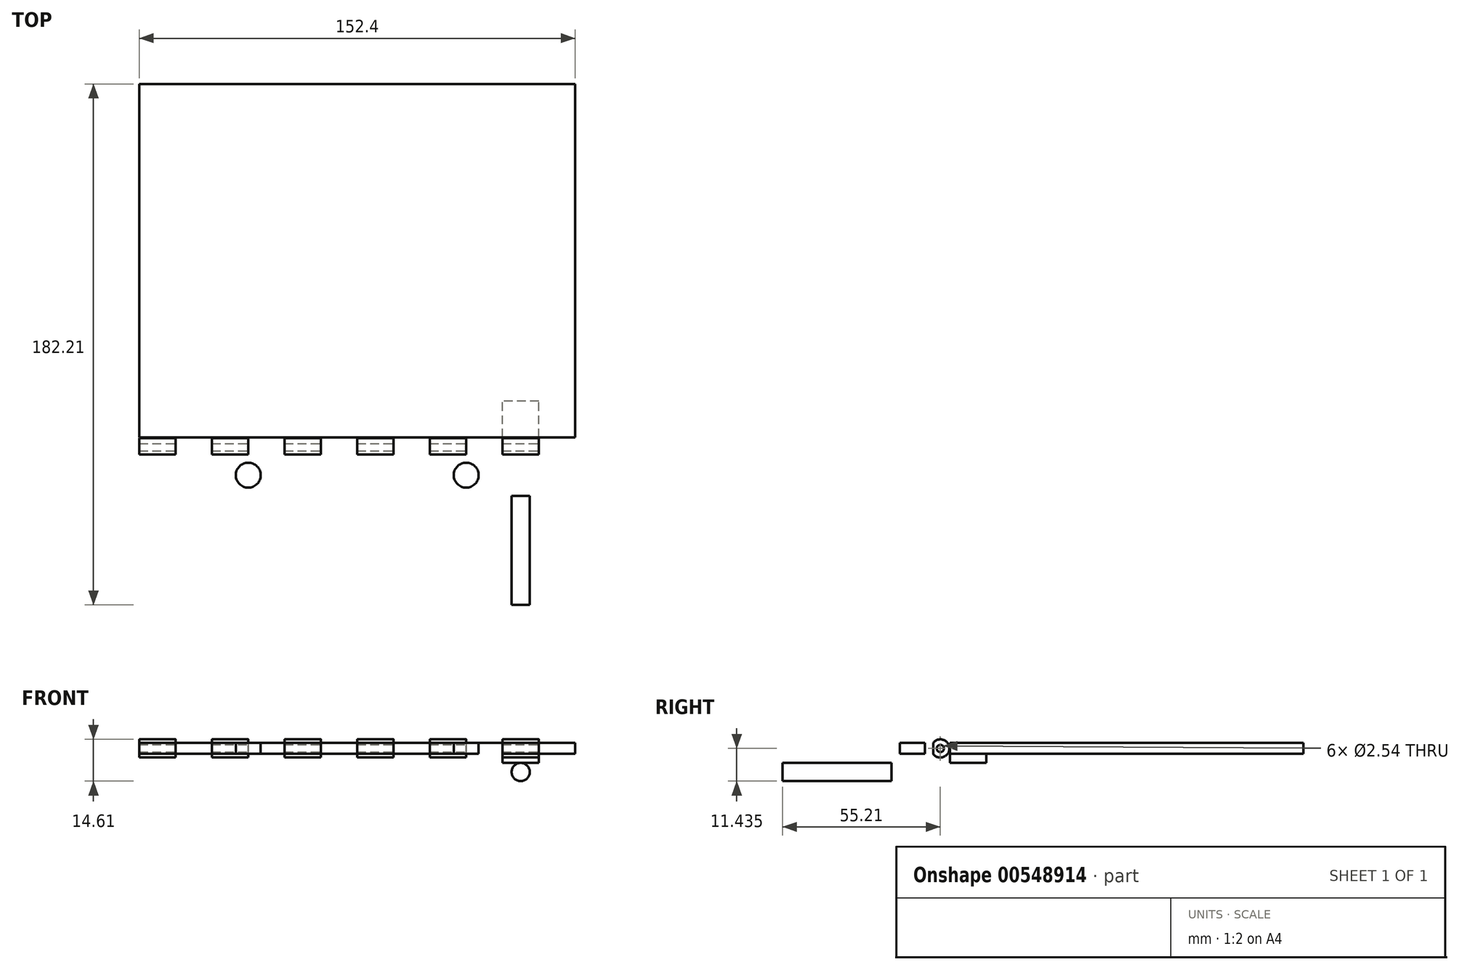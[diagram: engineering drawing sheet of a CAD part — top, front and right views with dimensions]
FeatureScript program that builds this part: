
annotation { "Feature Type Name" : "Feature", "Feature Type Description" : "" }
export const myFeature = defineFeature(function(context is Context, id is Id, definition is map)
    precondition{}
    {
        {
            var Q0;
            Q0=qCreatedBy(makeId("Top.planeOp"),FACE);
            var sketch = newSketch(context, id + "F0", { "sketchPlane" : qUnion([Q0])});
            skLineSegment(sketch, "E0.bottom", {"start": v(76.2, 63.5) * mm, "end": v(-76.2, 63.5) * mm});
            skLineSegment(sketch, "E0.top", {"start": v(76.2, -63.5) * mm, "end": v(-76.2, -63.5) * mm});
            skLineSegment(sketch, "E0.left", {"start": v(76.2, 63.5) * mm, "end": v(76.2, -63.5) * mm});
            skLineSegment(sketch, "E0.right", {"start": v(-76.2, 63.5) * mm, "end": v(-76.2, -63.5) * mm});
            skPoint(sketch, "E0.middle", {"position": v(0, 0) * mm});
            skSolve(sketch);
        }
        {
            var Q0;
            Q0=makeQuery(id+"F0.imprint","IMPRINT",FACE,{"disambiguationData":[TD([[makeQuery(id+"F0.imprint","IMPRINT",EDGE,{"derivedFrom":sQuery(id+"F0.wireOp",EDGE,"E0.bottom")}),1.0]])]});
            extrude(context, id + "F1", {"entities" : qUnion([Q0]), "depth" : 3.8 * mm, "offsetDistance" : 25.4 * mm});
        }
        {
            var Q0;
            Q0=makeQuery(id+"F1.opExtrude","SWEPT_FACE",FACE,{"disambiguationData":[OSD([sQuery(id+"F0.wireOp",EDGE,"E0.left")])]});
            var sketch = newSketch(context, id + "F2", { "sketchPlane" : qUnion([Q0])});
            skCircle(sketch, "E1", {"center": v(-63.5, 1.9) * mm, "radius": 3.18 * mm});
            skCircle(sketch, "E2", {"center": v(-63.5, 1.9) * mm, "radius": 1.27 * mm});
            skSolve(sketch);
        }
        {
            var Q0;
            {var subQ0=sQuery(id+"F2.wireOp",EDGE,"E2");var subQ1=makeQuery(id+"F1.opExtrude","SWEPT_EDGE",EDGE,{"disambiguationData":[OSD([sQuery(id+"F0.wireOp",EDGE,"E0.top"),sQuery(id+"F0.wireOp",EDGE,"E0.left")])]});var subQ2=makeQuery(id+"F2.imprint","INTERSECT",VERTEX,{"disambiguationData":[OD(0.0)],"derivedFrom":[subQ1,subQ0]});Q0=makeQuery(id+"F2.imprint","IMPRINT",FACE,{"disambiguationData":[TD([[makeQuery(id+"F2.imprint","IMPRINT",EDGE,{"disambiguationData":[TD([[subQ2,-1.0]])],"derivedFrom":subQ0}),1.0]])]});}
            extrude(context, id + "F3", {"entities" : qUnion([Q0]), "operationType" : NewBodyOperationType.REMOVE, "endBound" : BoundingType.THROUGH_ALL, "oppositeDirection" : true, "depth" : 25.4 * mm, "offsetDistance" : 25.4 * mm});
        }
        {
            var Q0;
            Q0 = qSketchRegion(id + "F2", true);
            var Q1;
            Q1=makeQuery(id+"F1.opExtrude","SWEPT_FACE",FACE,{"disambiguationData":[OSD([sQuery(id+"F0.wireOp",EDGE,"E0.right")])]});
            extrude(context, id + "F4", {"entities" : qUnion([Q0]), "operationType" : NewBodyOperationType.ADD, "endBound" : BoundingType.UP_TO_SURFACE, "oppositeDirection" : true, "depth" : 25.4 * mm, "endBoundEntityFace" : qUnion([Q1]), "offsetDistance" : 25.4 * mm});
        }
        {
            var Q0;
            Q0=qCreatedBy(makeId("Top.planeOp"),FACE);
            cPlane(context, id + "F5", {"entities" : qUnion([Q0]), "cplaneType" : CPlaneType.OFFSET, "offset" : 25.4 * mm, "width" : 152.4 * mm, "height" : 152.4 * mm});
        }
        {
            var Q0;
            Q0=qCreatedBy(id+"F5.planeOp",FACE);
            var sketch = newSketch(context, id + "F6", { "sketchPlane" : qUnion([Q0])});
            skLineSegment(sketch, "E3", {"start": v(63.5, -66.67) * mm, "end": v(50.8, -66.67) * mm});
            skLineSegment(sketch, "E4.0", {"start": v(-76.2, -60.96) * mm, "end": v(-76.2, -66.67) * mm});
            skLineSegment(sketch, "E5.bottom", {"start": v(-76.2, -66.67) * mm, "end": v(-63.5, -66.67) * mm});
            skLineSegment(sketch, "E5.top", {"start": v(-76.2, -60.07) * mm, "end": v(-63.5, -60.07) * mm});
            skLineSegment(sketch, "E5.left", {"start": v(-76.2, -66.67) * mm, "end": v(-76.2, -60.07) * mm});
            skLineSegment(sketch, "E5.right", {"start": v(-63.5, -66.67) * mm, "end": v(-63.5, -60.07) * mm});
            skLineSegment(sketch, "E6.1.0.0", {"start": v(-50.8, -60.07) * mm, "end": v(-38.1, -60.07) * mm});
            skLineSegment(sketch, "E6.1.0.1", {"start": v(-38.1, -66.67) * mm, "end": v(-38.1, -60.07) * mm});
            skLineSegment(sketch, "E6.1.0.2", {"start": v(-50.8, -66.67) * mm, "end": v(-38.1, -66.67) * mm});
            skLineSegment(sketch, "E6.1.0.3", {"start": v(-50.8, -66.67) * mm, "end": v(-50.8, -60.07) * mm});
            skLineSegment(sketch, "E6.2.0.0", {"start": v(-25.4, -60.07) * mm, "end": v(-12.7, -60.07) * mm});
            skLineSegment(sketch, "E6.2.0.1", {"start": v(-12.7, -66.67) * mm, "end": v(-12.7, -60.07) * mm});
            skLineSegment(sketch, "E6.2.0.2", {"start": v(-25.4, -66.67) * mm, "end": v(-12.7, -66.67) * mm});
            skLineSegment(sketch, "E6.2.0.3", {"start": v(-25.4, -66.67) * mm, "end": v(-25.4, -60.07) * mm});
            skLineSegment(sketch, "E6.3.0.0", {"start": v(0, -60.07) * mm, "end": v(12.7, -60.07) * mm});
            skLineSegment(sketch, "E6.3.0.1", {"start": v(12.7, -66.67) * mm, "end": v(12.7, -60.07) * mm});
            skLineSegment(sketch, "E6.3.0.2", {"start": v(0, -66.67) * mm, "end": v(12.7, -66.67) * mm});
            skLineSegment(sketch, "E6.3.0.3", {"start": v(0, -66.67) * mm, "end": v(0, -60.07) * mm});
            skLineSegment(sketch, "E6.4.0.0", {"start": v(25.4, -60.07) * mm, "end": v(38.1, -60.07) * mm});
            skLineSegment(sketch, "E6.4.0.1", {"start": v(38.1, -66.67) * mm, "end": v(38.1, -60.07) * mm});
            skLineSegment(sketch, "E6.4.0.2", {"start": v(25.4, -66.67) * mm, "end": v(38.1, -66.67) * mm});
            skLineSegment(sketch, "E6.4.0.3", {"start": v(25.4, -66.67) * mm, "end": v(25.4, -60.07) * mm});
            skLineSegment(sketch, "E6.5.0.0", {"start": v(50.8, -60.07) * mm, "end": v(63.5, -60.07) * mm});
            skLineSegment(sketch, "E6.5.0.1", {"start": v(63.5, -66.67) * mm, "end": v(63.5, -60.07) * mm});
            skLineSegment(sketch, "E6.5.0.2", {"start": v(50.8, -66.67) * mm, "end": v(63.5, -66.67) * mm});
            skLineSegment(sketch, "E6.5.0.3", {"start": v(50.8, -66.67) * mm, "end": v(50.8, -60.07) * mm});
            skLineSegment(sketch, "E6.direction1", {"start": v(-76.2, -60.07) * mm, "end": v(-63.5, -60.07) * mm, "construction": true});
            skPoint(sketch, "E7.0.start.orphan", {"position": v(76.2, -60.96) * mm});
            skPoint(sketch, "E8.0.end.orphan", {"position": v(76.2, -66.67) * mm});
            skLineSegment(sketch, "E9.trimOffspring", {"start": v(38.1, -66.67) * mm, "end": v(25.4, -66.67) * mm});
            skLineSegment(sketch, "E10.trimOffspring", {"start": v(12.7, -66.67) * mm, "end": v(0, -66.67) * mm});
            skLineSegment(sketch, "E11.trimOffspring", {"start": v(-12.7, -66.67) * mm, "end": v(-25.4, -66.67) * mm});
            skLineSegment(sketch, "E12.trimOffspring", {"start": v(-38.1, -66.67) * mm, "end": v(-50.8, -66.67) * mm});
            skLineSegment(sketch, "E13.trimOffspring", {"start": v(-63.5, -66.67) * mm, "end": v(-76.2, -66.67) * mm});
            skSolve(sketch);
        }
        {
            var Q0;
            Q0 = qSketchRegion(id + "F6", true);
            extrude(context, id + "F7", {"entities" : qUnion([Q0]), "operationType" : NewBodyOperationType.REMOVE, "endBound" : BoundingType.THROUGH_ALL, "oppositeDirection" : true, "depth" : 25.4 * mm, "offsetDistance" : 25.4 * mm});
        }
        {
            var Q0;
            Q0=makeQuery(id+"F4.boolean.opBoolean","MERGE",FACE,{"derivedFrom":[makeQuery(id+"F1.opExtrude","SWEPT_FACE",FACE,{"disambiguationData":[OSD([sQuery(id+"F0.wireOp",EDGE,"E0.left")])]}),makeQuery(id+"F4.opExtrude","CAP_FACE",FACE,{"disambiguationData":[OSD([sQuery(id+"F2.wireOp",EDGE,"E1"),sQuery(id+"F2.wireOp",EDGE,"E2")])],"isStart":true})]});
            var sketch = newSketch(context, id + "F8", { "sketchPlane" : qUnion([Q0])});
            skCircle(sketch, "E14.0", {"center": v(-63.5, 1.9) * mm, "radius": 1.27 * mm});
            skSolve(sketch);
        }
        {
            var Q0;
            Q0 = qSketchRegion(id + "F8", true);
            var Q1;
            {var subQ0=sQuery(id+"F0.wireOp",EDGE,"E0.right");Q1=makeQuery(id+"F4.boolean.opBoolean","MERGE",FACE,{"derivedFrom":[makeQuery(id+"F1.opExtrude","SWEPT_FACE",FACE,{"disambiguationData":[OSD([subQ0])]}),makeQuery(id+"F4.opExtrude","CAP_FACE",FACE,{"disambiguationData":[OSD([subQ0])],"isStart":false})]});}
            extrude(context, id + "F9", {"entities" : qUnion([Q0]), "endBound" : BoundingType.UP_TO_SURFACE, "oppositeDirection" : true, "depth" : 152.4 * mm, "endBoundEntityFace" : qUnion([Q1]), "offsetDistance" : 25.4 * mm});
        }
        {
            var Q0;
            Q0=qCreatedBy(makeId("Top.planeOp"),FACE);
            var sketch = newSketch(context, id + "F10", { "sketchPlane" : qUnion([Q0])});
            skLineSegment(sketch, "E15.0", {"start": v(-76.2, 63.5) * mm, "end": v(-76.2, -60.07) * mm});
            skLineSegment(sketch, "E16.0", {"start": v(76.2, 63.5) * mm, "end": v(76.2, -60.96) * mm});
            skLineSegment(sketch, "E17.bottom", {"start": v(-76.2, -61.96) * mm, "end": v(76.2, -61.96) * mm});
            skLineSegment(sketch, "E17.top", {"start": v(-76.2, -80.6) * mm, "end": v(76.2, -80.6) * mm});
            skLineSegment(sketch, "E17.left", {"start": v(-76.2, -61.96) * mm, "end": v(-76.2, -80.6) * mm});
            skLineSegment(sketch, "E17.right", {"start": v(76.2, -61.96) * mm, "end": v(76.2, -80.6) * mm});
            skSolve(sketch);
        }
        {
            var Q0;
            Q0=makeQuery(id+"F10.imprint","IMPRINT",FACE,{"disambiguationData":[TD([[makeQuery(id+"F10.imprint","IMPRINT",EDGE,{"derivedFrom":sQuery(id+"F10.wireOp",EDGE,"E17.bottom")}),-1.0]])]});
            extrude(context, id + "F11", {"entities" : qUnion([Q0]), "depth" : 3.8 * mm, "offsetDistance" : 25.4 * mm});
        }
        {
            var Q0;
            Q0=makeQuery(id+"F11.opExtrude","SWEPT_FACE",FACE,{"disambiguationData":[OSD([sQuery(id+"F10.wireOp",EDGE,"E17.right")])]});
            var sketch = newSketch(context, id + "F12", { "sketchPlane" : qUnion([Q0])});
            skCircle(sketch, "E18.0", {"center": v(-63.5, 1.9) * mm, "radius": 1.27 * mm});
            skArc(sketch, "E19.0", {"start": v(-60.96, 3.81) * mm, "mid": v(-66.67, 1.9) * mm, "end": v(-60.96, 0) * mm});
            skCircle(sketch, "E20", {"center": v(-63.5, 1.9) * mm, "radius": 3.18 * mm});
            skSolve(sketch);
        }
        {
            var Q0;
            {var subQ1=sQuery(id+"F10.wireOp",EDGE,"E17.right");var subQ6=makeQuery(id+"F11.opExtrude","SWEPT_EDGE",EDGE,{"disambiguationData":[OSD([sQuery(id+"F10.wireOp",EDGE,"E17.bottom"),subQ1])]});Q0=makeQuery(id+"F12.imprint","IMPRINT",FACE,{"disambiguationData":[TD([[makeQuery(id+"F12.imprint","IMPRINT",EDGE,{"derivedFrom":subQ6}),1.0]])]});}
            var Q1;
            Q1=makeQuery(id+"F11.opExtrude","SWEPT_FACE",FACE,{"disambiguationData":[OSD([sQuery(id+"F10.wireOp",EDGE,"E17.left")])]});
            extrude(context, id + "F13", {"entities" : qUnion([Q0]), "operationType" : NewBodyOperationType.ADD, "endBound" : BoundingType.UP_TO_SURFACE, "oppositeDirection" : true, "depth" : 25.4 * mm, "endBoundEntityFace" : qUnion([Q1]), "offsetDistance" : 25.4 * mm});
        }
        {
            var Q0;
            Q0=makeQuery(id+"F9.opExtrude","CAP_FACE",FACE,{"disambiguationData":[OSD([sQuery(id+"F8.wireOp",EDGE,"E14.0")])],"isStart":true});
            extrude(context, id + "F14", {"entities" : qUnion([Q0]), "operationType" : NewBodyOperationType.REMOVE, "endBound" : BoundingType.THROUGH_ALL, "oppositeDirection" : true, "depth" : 25.4 * mm, "offsetDistance" : 25.4 * mm});
        }
        {
            var Q0;
            Q0=qCreatedBy(id+"F5.planeOp",FACE);
            var sketch = newSketch(context, id + "F15", { "sketchPlane" : qUnion([Q0])});
            skPoint(sketch, "E21.0", {"position": v(76.2, -66.67) * mm});
            skPoint(sketch, "E22.0", {"position": v(63.5, -60.07) * mm});
            skPoint(sketch, "E23.0", {"position": v(50.8, -66.67) * mm});
            skPoint(sketch, "E24.0", {"position": v(38.1, -60.07) * mm});
            skPoint(sketch, "E25.0", {"position": v(25.4, -66.67) * mm});
            skPoint(sketch, "E26.0", {"position": v(12.7, -60.07) * mm});
            skPoint(sketch, "E27.0", {"position": v(0, -66.67) * mm});
            skPoint(sketch, "E28.0", {"position": v(-12.7, -60.07) * mm});
            skPoint(sketch, "E29.0", {"position": v(-25.4, -66.67) * mm});
            skPoint(sketch, "E30.0", {"position": v(-38.1, -60.07) * mm});
            skPoint(sketch, "E31.0", {"position": v(-50.8, -66.67) * mm});
            skPoint(sketch, "E32.0", {"position": v(-63.5, -60.07) * mm});
            skLineSegment(sketch, "E33.bottom", {"start": v(-63.5, -60.07) * mm, "end": v(-50.8, -60.07) * mm});
            skLineSegment(sketch, "E33.top", {"start": v(-63.5, -66.93) * mm, "end": v(-50.8, -66.93) * mm});
            skLineSegment(sketch, "E33.left", {"start": v(-63.5, -60.07) * mm, "end": v(-63.5, -66.93) * mm});
            skLineSegment(sketch, "E33.right", {"start": v(-50.8, -60.07) * mm, "end": v(-50.8, -66.93) * mm});
            skLineSegment(sketch, "E34.1.0.0", {"start": v(-38.1, -60.07) * mm, "end": v(-25.4, -60.07) * mm});
            skLineSegment(sketch, "E34.1.0.1", {"start": v(-25.4, -60.07) * mm, "end": v(-25.4, -66.93) * mm});
            skLineSegment(sketch, "E34.1.0.2", {"start": v(-38.1, -66.93) * mm, "end": v(-25.4, -66.93) * mm});
            skLineSegment(sketch, "E34.1.0.3", {"start": v(-38.1, -60.07) * mm, "end": v(-38.1, -66.93) * mm});
            skLineSegment(sketch, "E34.2.0.0", {"start": v(-12.7, -60.07) * mm, "end": v(0, -60.07) * mm});
            skLineSegment(sketch, "E34.2.0.1", {"start": v(0, -60.07) * mm, "end": v(0, -66.93) * mm});
            skLineSegment(sketch, "E34.2.0.2", {"start": v(-12.7, -66.93) * mm, "end": v(0, -66.93) * mm});
            skLineSegment(sketch, "E34.2.0.3", {"start": v(-12.7, -60.07) * mm, "end": v(-12.7, -66.93) * mm});
            skLineSegment(sketch, "E34.3.0.0", {"start": v(12.7, -60.07) * mm, "end": v(25.4, -60.07) * mm});
            skLineSegment(sketch, "E34.3.0.1", {"start": v(25.4, -60.07) * mm, "end": v(25.4, -66.93) * mm});
            skLineSegment(sketch, "E34.3.0.2", {"start": v(12.7, -66.93) * mm, "end": v(25.4, -66.93) * mm});
            skLineSegment(sketch, "E34.3.0.3", {"start": v(12.7, -60.07) * mm, "end": v(12.7, -66.93) * mm});
            skLineSegment(sketch, "E34.4.0.0", {"start": v(38.1, -60.07) * mm, "end": v(50.8, -60.07) * mm});
            skLineSegment(sketch, "E34.4.0.1", {"start": v(50.8, -60.07) * mm, "end": v(50.8, -66.93) * mm});
            skLineSegment(sketch, "E34.4.0.2", {"start": v(38.1, -66.93) * mm, "end": v(50.8, -66.93) * mm});
            skLineSegment(sketch, "E34.4.0.3", {"start": v(38.1, -60.07) * mm, "end": v(38.1, -66.93) * mm});
            skLineSegment(sketch, "E34.5.0.0", {"start": v(63.5, -60.07) * mm, "end": v(76.2, -60.07) * mm});
            skLineSegment(sketch, "E34.5.0.1", {"start": v(76.2, -60.07) * mm, "end": v(76.2, -66.93) * mm});
            skLineSegment(sketch, "E34.5.0.2", {"start": v(63.5, -66.93) * mm, "end": v(76.2, -66.93) * mm});
            skLineSegment(sketch, "E34.5.0.3", {"start": v(63.5, -60.07) * mm, "end": v(63.5, -66.93) * mm});
            skLineSegment(sketch, "E34.direction1", {"start": v(-63.5, -60.07) * mm, "end": v(-38.1, -60.07) * mm, "construction": true});
            skSolve(sketch);
        }
        {
            var Q0;
            Q0 = qSketchRegion(id + "F15", true);
            extrude(context, id + "F16", {"entities" : qUnion([Q0]), "operationType" : NewBodyOperationType.REMOVE, "endBound" : BoundingType.THROUGH_ALL, "oppositeDirection" : true, "depth" : 25.4 * mm, "offsetDistance" : 25.4 * mm});
        }
        {
            var Q0;
            Q0=makeQuery(id+"F11.opExtrude","SWEPT_FACE",FACE,{"disambiguationData":[OSD([sQuery(id+"F10.wireOp",EDGE,"E17.top")])]});
            var sketch = newSketch(context, id + "F17", { "sketchPlane" : qUnion([Q0])});
            skArc(sketch, "E35", {"start": v(50.8, -6.35) * mm, "mid": v(57.15, -12.7) * mm, "end": v(63.5, -6.35) * mm});
            skLineSegment(sketch, "E36", {"start": v(63.5, -6.35) * mm, "end": v(63.5, 0) * mm});
            skLineSegment(sketch, "E37", {"start": v(50.8, -6.35) * mm, "end": v(50.8, 0) * mm});
            skCircle(sketch, "E38", {"center": v(57.15, -6.35) * mm, "radius": 3.18 * mm});
            skSolve(sketch);
        }
        {
            var Q0;
            Q0=makeQuery(id+"F17.imprint","IMPRINT",FACE,{"disambiguationData":[TD([[makeQuery(id+"F17.imprint","IMPRINT",EDGE,{"derivedFrom":sQuery(id+"F17.wireOp",EDGE,"E35")}),1.0]])]});
            extrude(context, id + "F18", {"entities" : qUnion([Q0]), "operationType" : NewBodyOperationType.ADD, "oppositeDirection" : true, "depth" : 12.7 * mm, "offsetDistance" : 25.4 * mm});
        }
        {
            var Q0;
            Q0=makeQuery(id+"F1.opExtrude","CAP_FACE",FACE,{"disambiguationData":[OSD([sQuery(id+"F0.wireOp",EDGE,"E0.bottom"),sQuery(id+"F0.wireOp",EDGE,"E0.top"),sQuery(id+"F0.wireOp",EDGE,"E0.left"),sQuery(id+"F0.wireOp",EDGE,"E0.right")])],"isStart":true});
            var sketch = newSketch(context, id + "F19", { "sketchPlane" : qUnion([Q0])});
            skLineSegment(sketch, "E39.bottom", {"start": v(63.5, 60.07) * mm, "end": v(50.8, 60.07) * mm});
            skLineSegment(sketch, "E39.top", {"start": v(63.5, 47.37) * mm, "end": v(50.8, 47.37) * mm});
            skLineSegment(sketch, "E39.left", {"start": v(63.5, 60.07) * mm, "end": v(63.5, 47.37) * mm});
            skLineSegment(sketch, "E39.right", {"start": v(50.8, 60.07) * mm, "end": v(50.8, 47.37) * mm});
            skSolve(sketch);
        }
        {
            var Q0;
            Q0=makeQuery(id+"F19.imprint","IMPRINT",FACE,{"disambiguationData":[TD([[makeQuery(id+"F19.imprint","IMPRINT",EDGE,{"derivedFrom":sQuery(id+"F19.wireOp",EDGE,"E39.bottom")}),-1.0]])]});
            extrude(context, id + "F20", {"entities" : qUnion([Q0]), "operationType" : NewBodyOperationType.ADD, "depth" : 3.17 * mm, "offsetDistance" : 25.4 * mm});
        }
        {
            var Q0;
            Q0=qCreatedBy(id+"F5.planeOp",FACE);
            var sketch = newSketch(context, id + "F21", { "sketchPlane" : qUnion([Q0])});
            skLineSegment(sketch, "E40.0.0", {"start": v(-63.5, -66.93) * mm, "end": v(-63.5, -66.04) * mm});
            skLineSegment(sketch, "E40.0.1", {"start": v(-63.5, -66.04) * mm, "end": v(-76.2, -66.04) * mm});
            skLineSegment(sketch, "E40.0.2", {"start": v(-76.2, -66.04) * mm, "end": v(-76.2, -80.6) * mm});
            skLineSegment(sketch, "E40.0.3", {"start": v(-76.2, -80.6) * mm, "end": v(76.2, -80.6) * mm});
            skLineSegment(sketch, "E40.0.4", {"start": v(76.2, -80.6) * mm, "end": v(76.2, -66.93) * mm});
            skLineSegment(sketch, "E40.0.5", {"start": v(76.2, -66.93) * mm, "end": v(63.5, -66.93) * mm});
            skLineSegment(sketch, "E40.0.6", {"start": v(63.5, -66.93) * mm, "end": v(63.5, -66.04) * mm});
            skLineSegment(sketch, "E40.0.7", {"start": v(63.5, -66.04) * mm, "end": v(50.8, -66.04) * mm});
            skLineSegment(sketch, "E40.0.8", {"start": v(50.8, -66.04) * mm, "end": v(50.8, -66.93) * mm});
            skLineSegment(sketch, "E40.0.9", {"start": v(50.8, -66.93) * mm, "end": v(38.1, -66.93) * mm});
            skLineSegment(sketch, "E40.0.10", {"start": v(38.1, -66.93) * mm, "end": v(38.1, -66.04) * mm});
            skLineSegment(sketch, "E40.0.11", {"start": v(38.1, -66.04) * mm, "end": v(25.4, -66.04) * mm});
            skLineSegment(sketch, "E40.0.12", {"start": v(25.4, -66.04) * mm, "end": v(25.4, -66.93) * mm});
            skLineSegment(sketch, "E40.0.13", {"start": v(25.4, -66.93) * mm, "end": v(12.7, -66.93) * mm});
            skLineSegment(sketch, "E40.0.14", {"start": v(12.7, -66.93) * mm, "end": v(12.7, -66.04) * mm});
            skLineSegment(sketch, "E40.0.15", {"start": v(12.7, -66.04) * mm, "end": v(0, -66.04) * mm});
            skLineSegment(sketch, "E40.0.16", {"start": v(0, -66.04) * mm, "end": v(0, -66.93) * mm});
            skLineSegment(sketch, "E40.0.17", {"start": v(0, -66.93) * mm, "end": v(-12.7, -66.93) * mm});
            skLineSegment(sketch, "E40.0.18", {"start": v(-12.7, -66.93) * mm, "end": v(-12.7, -66.04) * mm});
            skLineSegment(sketch, "E40.0.19", {"start": v(-12.7, -66.04) * mm, "end": v(-25.4, -66.04) * mm});
            skLineSegment(sketch, "E40.0.20", {"start": v(-25.4, -66.04) * mm, "end": v(-25.4, -66.93) * mm});
            skLineSegment(sketch, "E40.0.21", {"start": v(-25.4, -66.93) * mm, "end": v(-38.1, -66.93) * mm});
            skLineSegment(sketch, "E40.0.22", {"start": v(-38.1, -66.93) * mm, "end": v(-38.1, -66.04) * mm});
            skLineSegment(sketch, "E40.0.23", {"start": v(-38.1, -66.04) * mm, "end": v(-50.8, -66.04) * mm});
            skLineSegment(sketch, "E40.0.24", {"start": v(-50.8, -66.04) * mm, "end": v(-50.8, -66.93) * mm});
            skLineSegment(sketch, "E40.0.25", {"start": v(-50.8, -66.93) * mm, "end": v(-63.5, -66.93) * mm});
            skLineSegment(sketch, "E41", {"start": v(-76.2, -73.32) * mm, "end": v(76.2, -73.32) * mm});
            skCircle(sketch, "E42", {"center": v(-38.1, -73.32) * mm, "radius": 4.37 * mm});
            skCircle(sketch, "E43", {"center": v(38.1, -73.32) * mm, "radius": 4.37 * mm});
            skSolve(sketch);
        }
        {
            var Q0;
            Q0=makeQuery(id+"F18.opExtrude","CAP_FACE",FACE,{"disambiguationData":[OSD([sQuery(id+"F10.wireOp",EDGE,"E17.top"),sQuery(id+"F17.wireOp",EDGE,"E35"),sQuery(id+"F17.wireOp",EDGE,"E36"),sQuery(id+"F17.wireOp",EDGE,"E37"),sQuery(id+"F17.wireOp",EDGE,"E38")])],"isStart":false});
            var sketch = newSketch(context, id + "F22", { "sketchPlane" : qUnion([Q0])});
            skCircle(sketch, "E44", {"center": v(-57.15, -6.35) * mm, "radius": 3.17 * mm});
            skPoint(sketch, "E44.first.point", {"position": v(-56.95, -9.52) * mm});
            skPoint(sketch, "E44.second.point", {"position": v(-60.18, -7.3) * mm});
            skPoint(sketch, "E44.third.point", {"position": v(-55, -4.01) * mm});
            skSolve(sketch);
        }
        {
            var Q0;
            Q0=makeQuery(id+"F22.imprint","IMPRINT",FACE,{"disambiguationData":[TD([[makeQuery(id+"F22.imprint","IMPRINT",EDGE,{"derivedFrom":sQuery(id+"F22.wireOp",EDGE,"E44")}),-1.0]])]});
            extrude(context, id + "F23", {"entities" : qUnion([Q0]), "oppositeDirection" : true, "depth" : 50.8 * mm, "offsetDistance" : 25.4 * mm});
        }
        {
            var Q0;
            {var subQ0=sQuery(id+"F21.wireOp",EDGE,"E42");var subQ1=sQuery(id+"F21.wireOp",EDGE,"E41");var subQ2=makeQuery(id+"F21.imprint","INTERSECT",VERTEX,{"disambiguationData":[OD(0.0)],"derivedFrom":[subQ1,subQ0]});Q0=makeQuery(id+"F21.imprint","IMPRINT",FACE,{"disambiguationData":[TD([[makeQuery(id+"F21.imprint","IMPRINT",EDGE,{"disambiguationData":[TD([[subQ2,-1.0]])],"derivedFrom":subQ1}),-1.0]])]});}
            var Q1;
            {var subQ0=sQuery(id+"F21.wireOp",EDGE,"E42");var subQ1=sQuery(id+"F21.wireOp",EDGE,"E41");var subQ2=makeQuery(id+"F21.imprint","INTERSECT",VERTEX,{"disambiguationData":[OD(0.0)],"derivedFrom":[subQ1,subQ0]});Q1=makeQuery(id+"F21.imprint","IMPRINT",FACE,{"disambiguationData":[TD([[makeQuery(id+"F21.imprint","IMPRINT",EDGE,{"disambiguationData":[TD([[subQ2,-1.0]])],"derivedFrom":subQ1}),1.0]])]});}
            var Q2;
            {var subQ0=sQuery(id+"F21.wireOp",EDGE,"E43");var subQ1=sQuery(id+"F21.wireOp",EDGE,"E41");var subQ2=makeQuery(id+"F21.imprint","INTERSECT",VERTEX,{"disambiguationData":[OD(0.0)],"derivedFrom":[subQ1,subQ0]});Q2=makeQuery(id+"F21.imprint","IMPRINT",FACE,{"disambiguationData":[TD([[makeQuery(id+"F21.imprint","IMPRINT",EDGE,{"disambiguationData":[TD([[subQ2,-1.0]])],"derivedFrom":subQ1}),1.0]])]});}
            var Q3;
            {var subQ0=sQuery(id+"F21.wireOp",EDGE,"E43");var subQ1=sQuery(id+"F21.wireOp",EDGE,"E41");var subQ2=makeQuery(id+"F21.imprint","INTERSECT",VERTEX,{"disambiguationData":[OD(0.0)],"derivedFrom":[subQ1,subQ0]});Q3=makeQuery(id+"F21.imprint","IMPRINT",FACE,{"disambiguationData":[TD([[makeQuery(id+"F21.imprint","IMPRINT",EDGE,{"disambiguationData":[TD([[subQ2,-1.0]])],"derivedFrom":subQ1}),-1.0]])]});}
            extrude(context, id + "F24", {"entities" : qUnion([Q0, Q1, Q2, Q3]), "operationType" : NewBodyOperationType.REMOVE, "endBound" : BoundingType.THROUGH_ALL, "oppositeDirection" : true, "depth" : 25.4 * mm, "offsetDistance" : 25.4 * mm});
        }
    });
